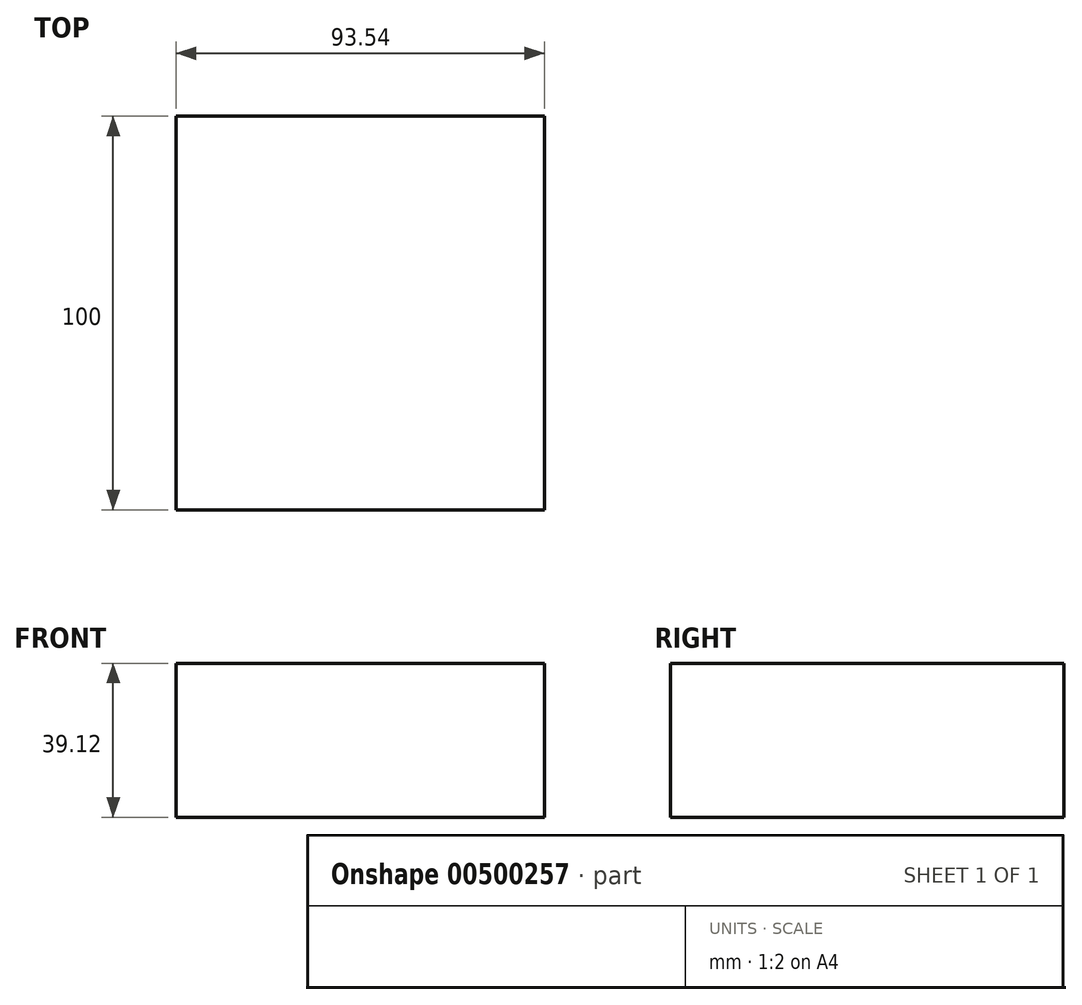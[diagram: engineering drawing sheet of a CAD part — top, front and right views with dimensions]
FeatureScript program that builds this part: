
annotation { "Feature Type Name" : "Feature", "Feature Type Description" : "" }
export const myFeature = defineFeature(function(context is Context, id is Id, definition is map)
    precondition{}
    {
        {
            var Q0;
            Q0=qCreatedBy(makeId("Front.planeOp"),FACE);
            var sketch = newSketch(context, id + "F0", { "sketchPlane" : qUnion([Q0])});
            skLineSegment(sketch, "E0.bottom", {"start": v(46.77, -19.56) * mm, "end": v(-46.77, -19.56) * mm});
            skLineSegment(sketch, "E0.top", {"start": v(46.77, 19.56) * mm, "end": v(-46.77, 19.56) * mm});
            skLineSegment(sketch, "E0.left", {"start": v(46.77, -19.56) * mm, "end": v(46.77, 19.56) * mm});
            skLineSegment(sketch, "E0.right", {"start": v(-46.77, -19.56) * mm, "end": v(-46.77, 19.56) * mm});
            skPoint(sketch, "E0.middle", {"position": v(0, 0) * mm});
            skSolve(sketch);
        }
        {
            var Q0;
            Q0=makeQuery(id+"F0.imprint","IMPRINT",FACE,{"disambiguationData":[TD([[makeQuery(id+"F0.imprint","IMPRINT",EDGE,{"derivedFrom":sQuery(id+"F0.wireOp",EDGE,"E0.bottom")}),-1.0]])]});
            extrude(context, id + "F1", {"entities" : qUnion([Q0]), "depth" : 100 * mm});
        }
    });
